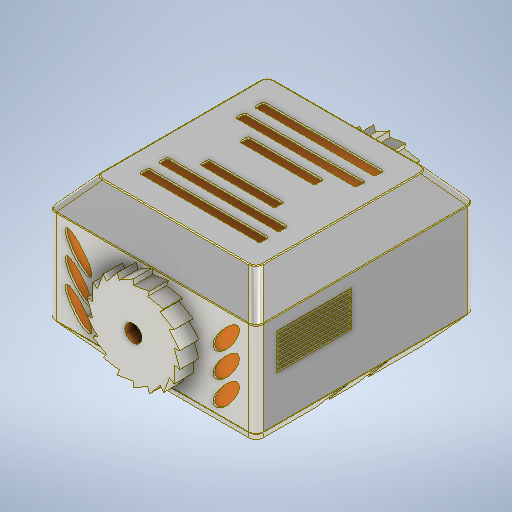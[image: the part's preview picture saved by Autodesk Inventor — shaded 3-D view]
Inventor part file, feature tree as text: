
AUTODESK INVENTOR PART (.ipt)
format: ipt  version: 2025 (Build 290162000, 162)  size: 1,108,480 bytes
history: native  units: in
note: dims shown in document units (in); Inventor stores cm internally (conversion verified against a paired STEP export)
features: sketch x17, fillet x14, extrude x10, mirror x3, emboss x1
ambient origin geometry x8: Origin, YZ Plane, XZ Plane, XY Plane, X Axis, Y Axis, Z Axis, Center Point
bodies: Solid1 (feature_tree)
feature tree (45):
  extrude  "Extrusion1"  Depth=4.3307in
  extrude  "Extrusion3"  Depth=1.9685in TaperAngle=0.0deg
  extrude  "Extrusion4"  Depth=1.9685in
  sketch  "Sketch11"  dims[d74=1.5748in d76=0.3937in d77=0.3937in d79=0.3937in d81=0.1811in d82=0.2598in d85=0.2598in d86=0.1811in]
  sketch  "Sketch15"  dims[d87=1.5748in d89=0.3937in d90=0.3937in d92=0.3937in d94=0.0394in d95=0.0in d96=0.0984in]
  extrude  "Extrusion12"  Depth=2.9921in
  extrude  "Extrusion13"  Depth=0.3937in
  extrude  "Extrusion14"  Depth=0.3937in
  fillet  "Fillet1"  Radius=0.3937in
  fillet  "Fillet2"  Radius=0.2362in
  fillet  "Fillet3"  Radius=0.1575in
  fillet  "Fillet4"  Radius=0.315in
  extrude  "Extrusion15"  Depth=0.5906in TaperAngle=0.0deg
  extrude  "Extrusion16"  Depth=0.0984in
  fillet  "Fillet5"  Radius=0.0984in
  fillet  "Fillet6"  Radius=0.0984in
  fillet  "Fillet7"  Radius=0.1181in
  fillet  "Fillet8"  Radius=7.0866in
  mirror  "Mirror1"
  fillet  "Fillet9"  Radius=0.3937in
  extrude  "Extrusion17"  Depth=0.2126in
  mirror  "Mirror3"
  mirror  "Mirror4"
  sketch  "Sketch20"  dims[d100=0.315in]
  extrude  "Extrusion18"  Depth=0.1811in
  fillet  "Fillet10"  Radius=0.2598in
  fillet  "Fillet11"  Radius=0.2598in
  fillet  "Fillet12"  Radius=0.1811in
  fillet  "Fillet14"  Radius=0.0394in
  emboss  "Emboss1"
  fillet  "Fillet15"  Radius=0.0984in
  sketch  "Sketch1"  dims[d0=4.5669in d1=4.3307in]
  sketch  "Sketch6"  dims[d61=0.0984in d62=0.0984in d63=0.0984in d64=0.0984in d65=0.1181in d66=7.0866in d68=360.0deg d70=0.3937in d71=0.0in]
  sketch  "Sketch7"  dims[d72=0.2362in d73=0.2126in]
  sketch  "Sketch17"  dims[d97=0.0984in]
  sketch  "Sketch Circular Pattern1"  dims[d2=0.5906in d3=-0.2749in d15=1.9685in d16=0.0in]
  sketch  "Sketch Rectangular Pattern1"  dims[d17=0.5906in d18=-0.2749in d30=1.9685in]
  sketch  "Sketch18"  dims[d98=0.0984in]
  sketch  "Sketch Rectangular Pattern2"  dims[d36=0.3543in d45=2.9921in]
  sketch  "Sketch19"  dims[d99=0.1575in]
  sketch  "Sketch Rectangular Pattern3"  dims[d46=1.1811in d47=0.3937in]
  sketch  "Sketch21"  dims[d101=0.1969in]
  sketch  "Sketch Rectangular Pattern4"  dims[d48=0.3937in d49=2.2047in d50=0.3937in d51=0.2362in d52=0.0in d53=0.1575in d54=0.0in d57=0.315in]
  sketch  "Sketch22"  dims[d102=0.1575in d103=0.2362in d104=1.1811in d106=0.5118in d107=0.3937in d109=0.3937in d111=0.0394in d112=0.0in d113=0.2756in d114=0.2677in d115=1.5748in d116=0.0472in d117=3.937in d119=0.0787in d120=0.3937in d122=0.3937in d124=0.0394in d125=0.0in d126=0.0315in d127=0.0315in d128=0.0315in d130=0.0295in d131=0.1969in d132=0.1969in d133=0.1969in d134=0.1969in d135=0.1969in d136=1.2598in d138=0.0394in d139=0.0394in d141=0.315in d142=0.0394in d143=0.0in d144=1.5748in d146=0.3937in d147=0.3937in d149=0.3937in d151=0.0394in d152=0.0197in d55=0.0197in d56=0.0344in d129=0.0in d145=0.0in]
  sketch  "Sketch Rectangular Pattern5"  dims[d58=0.1969in d59=0.5906in d60=0.0in]
